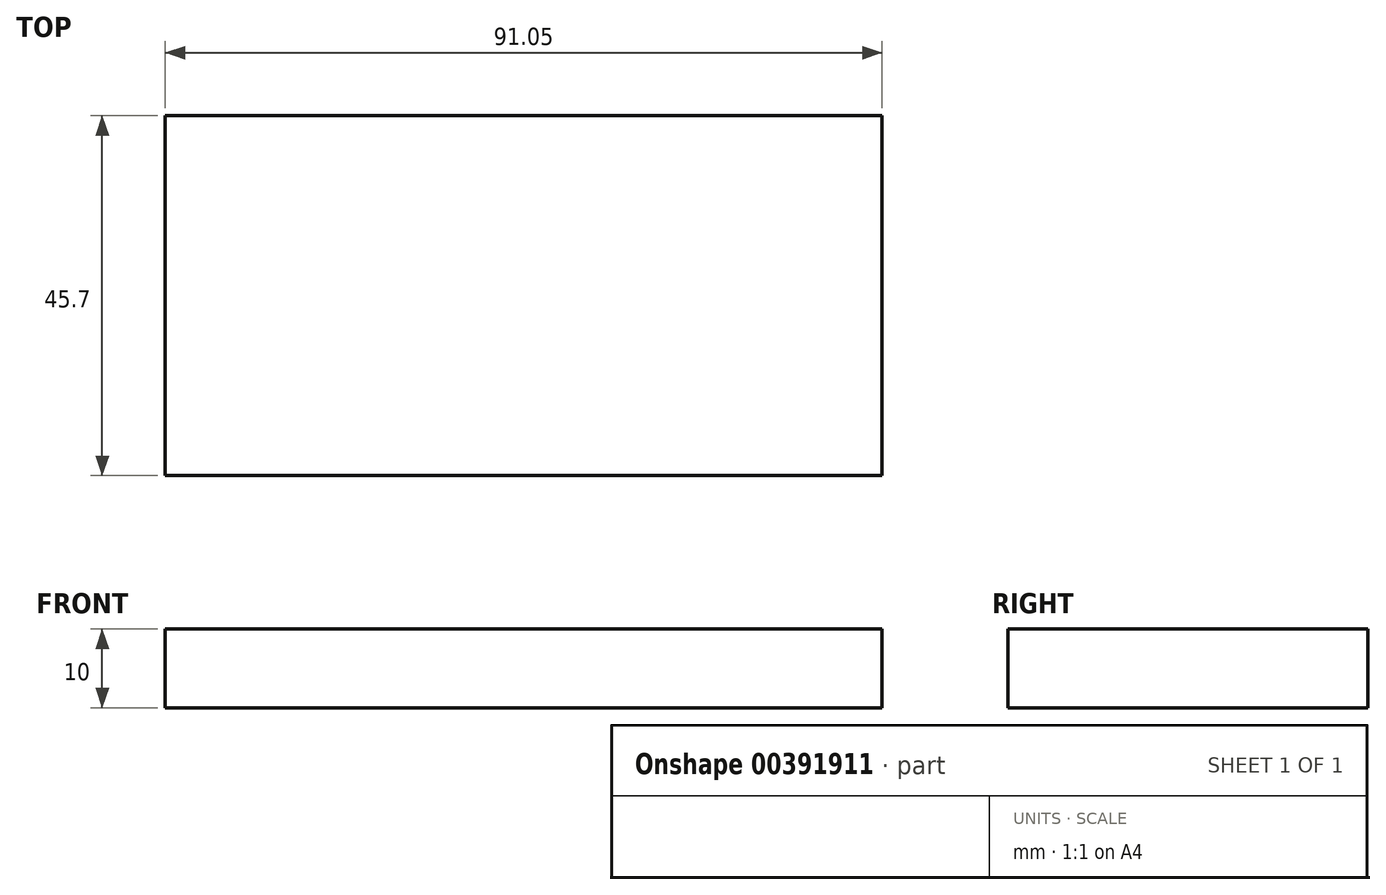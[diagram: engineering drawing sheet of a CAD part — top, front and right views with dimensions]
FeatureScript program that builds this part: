
annotation { "Feature Type Name" : "Feature", "Feature Type Description" : "" }
export const myFeature = defineFeature(function(context is Context, id is Id, definition is map)
    precondition{}
    {
        {
            var Q0;
            Q0=qCreatedBy(makeId("Top.planeOp"),FACE);
            var sketch = newSketch(context, id + "F0", { "sketchPlane" : qUnion([Q0])});
            skLineSegment(sketch, "E0.bottom", {"start": v(-56.71, 0) * mm, "end": v(34.34, 0) * mm});
            skLineSegment(sketch, "E0.top", {"start": v(-56.71, -45.7) * mm, "end": v(34.34, -45.7) * mm});
            skLineSegment(sketch, "E0.left", {"start": v(-56.71, 0) * mm, "end": v(-56.71, -45.7) * mm});
            skLineSegment(sketch, "E0.right", {"start": v(34.34, 0) * mm, "end": v(34.34, -45.7) * mm});
            skSolve(sketch);
        }
        {
            var Q0;
            Q0 = qSketchRegion(id + "F0", true);
            extrude(context, id + "F1", {"entities" : qUnion([Q0]), "depth" : 10 * mm});
        }
    });
